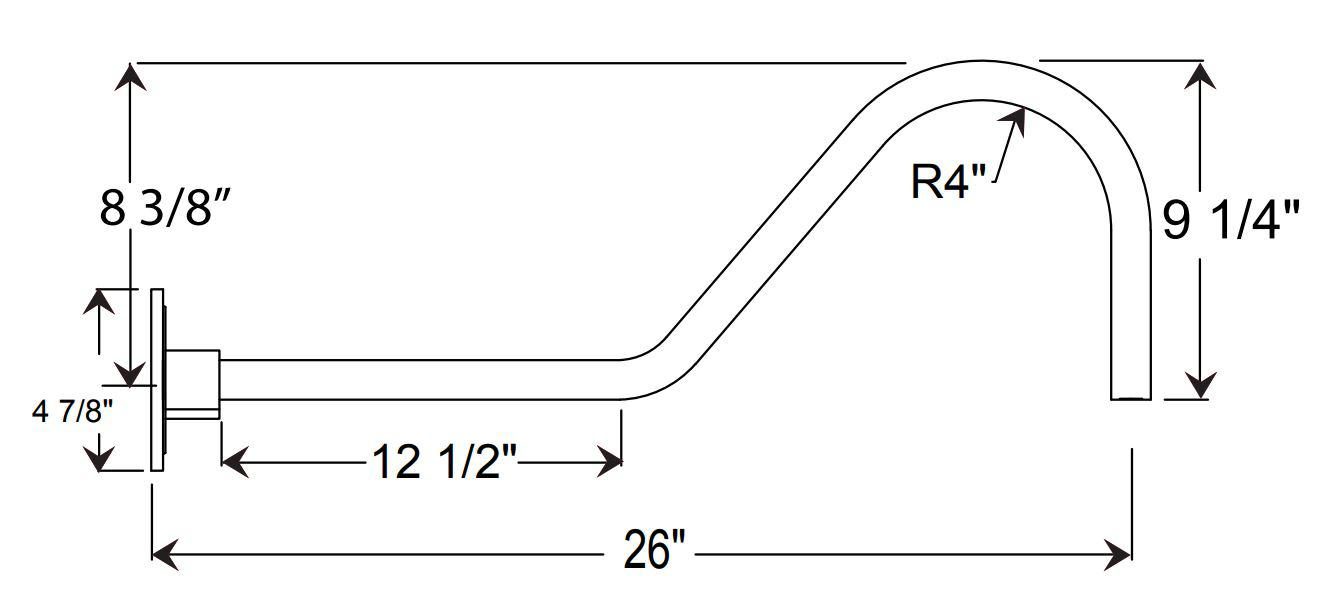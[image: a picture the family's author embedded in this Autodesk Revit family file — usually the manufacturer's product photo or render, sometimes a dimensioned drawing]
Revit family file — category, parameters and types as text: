
# Revit family: BULLET(8,10,12,16,20)MB
name_source: partatom
category: Lighting Fixtures
units: mm (PartAtom-declared; Revit-internal decimal feet)

## family parameters
Always vertical = Yes
Cut with Voids When Loaded = No
Light Source = Yes
OmniClass Number = 23.80.70.00
OmniClass Title = Lighting
Part Type = Normal
Room Calculation Point = No
Round Connector Dimension = Use Diameter
Shared = No
Work Plane-Based = No

## types (3) — shared parameters
Apparent Load = 200 VA
Body Colour = Spun aluminium
Body Material = body
Bulb = Bulb
CRI = >90
Color Filter = 16777215
Construction Material = Heavy Duty spun aluminum.
Default Elevation = 0' - 0"
Description = 120-277 Voltage
Dimming = 1%
Dimming Lamp Color Temperature Shift = <None>
Efficiency = 97-125 lumens per watt
INSIDE BODY = INSIDE BODY
Lamp = MB
Life = L70 50,000 hours
Load Classification = Lighting
Manufacturer = ANP Lighting
Photometric Web File = generic.ies
Power Factor = 1
Tilt Angle = 90.00°
URL = https://www.anplighting.com
Voltage = 277 V
Warranty = 5 year limited warranty
Wattage Comments = 200W Max

## per-type parameters (varying)
| type | Fixture Diameter | Fixture Height | GG12 | GG16 | GG20 | Weight |
| GG12 | 1' - 0" | 1' - 1" | Yes | No | No | 3.0lbs |
| GG16 | 16' - 0" | 1' - 5 1/2" | No | Yes | No | 6.0lbs |
| GG20 | 1' - 8" | 1' - 9" | No | No | Yes | 9.0lbs |

note: column(s) folded — value = type name in every type: Model

## geometry (parser evidence)
native form markers: Sweep x35
no freeform markers — native parametric forms only
